# Revit family: QF_BOURGEAT_Satellite4GT_froid_2-1_vitree_ouverture_gauche
name_source: partatom
category: Equipement spécialisé
revit_build: Autodesk Revit 2015 (Build: 20140606_1530(x64)
units: mm (PartAtom-declared; Revit-internal decimal feet)

## types (1)
- GN40_tirant_gauche
    Certification = NF hygiene alimentaire
    Charge max = 300.00 kg
    Charge_gaz = 0.220 Kg
    Classe Climatique = 4
    Consommation énergétique = 4.3 Kwh/h NFD40-016
    Diametre_roue = 160 mm  [stored 0.524934 ft]
    Dimension_verticale_vitre = 704 mm  [stored 2.30971 ft]
    Fabricant = BOURGEAT
    Frequence = 50/60 Hz
    Hauteur hors tout = 1876 mm
    Hauteur_poignee_porte_sol = 816 mm
    Hauteur_poignees_laterales = 906 mm  [stored 2.97244 ft]
    Hauteur_porte = 1629 mm  [stored 5.34449 ft]
    Hauteur_roue = 200 mm  [stored 0.656168 ft]
    Indice de protection = IP25
    Intensite = 2 A
    Largeur_porte = 706 mm  [stored 2.31627 ft]
    Longueur hors tout = 791 mm
    Longueur_poignees_laterales = 973 mm  [stored 3.19226 ft]
    Materiau_Poignee_porte = B_Elastomère_TPE_S
    Materiau_bac = B_Elastomère_TPE_S
    Materiau_bandage = B_Elastomère_TPE_S
    Materiau_glissiere = Acrylique, transparent
    Materiau_porte = Acier inoxydable, brossé
    Materiau_vitre = Verre, vitrage transparent, trempé
    Modèle = 842740
    Nature isolant = Mousse sans PU
    Phase = 2
    Poids net à vide = 160.00 kg
    Pos_IHM_bord_gauche_porte_droite = 526 mm  [stored 1.72572 ft]
    Pos_IHM_bord_gauche_porte_gauche = 175 mm  [stored 0.574147 ft]
    Pos_V_IHM = 98 mm  [stored 0.321522 ft]
    Pos_vitre_bord_gauche_porte_droite = 103 mm  [stored 0.337927 ft]
    Pos_vitre_bord_gauche_porte_gauche = 350 mm  [stored 1.14829 ft]
    Profondeur hors tout = 1129 mm  [stored 3.70407 ft]
    Puissance frigorifique = 465 W à -5°C
    Puissance électrique  = 500 W
    Spécification du Fabricant = Satellite 4GT
    Tension = 230 V
    Type Fluide Frigorigène = R134a
    URL catalogue = http://www.bourgeat.fr

note: [stored X ft] marks values corroborated as IEEE doubles in the binary element streams (Revit-internal decimal feet)
